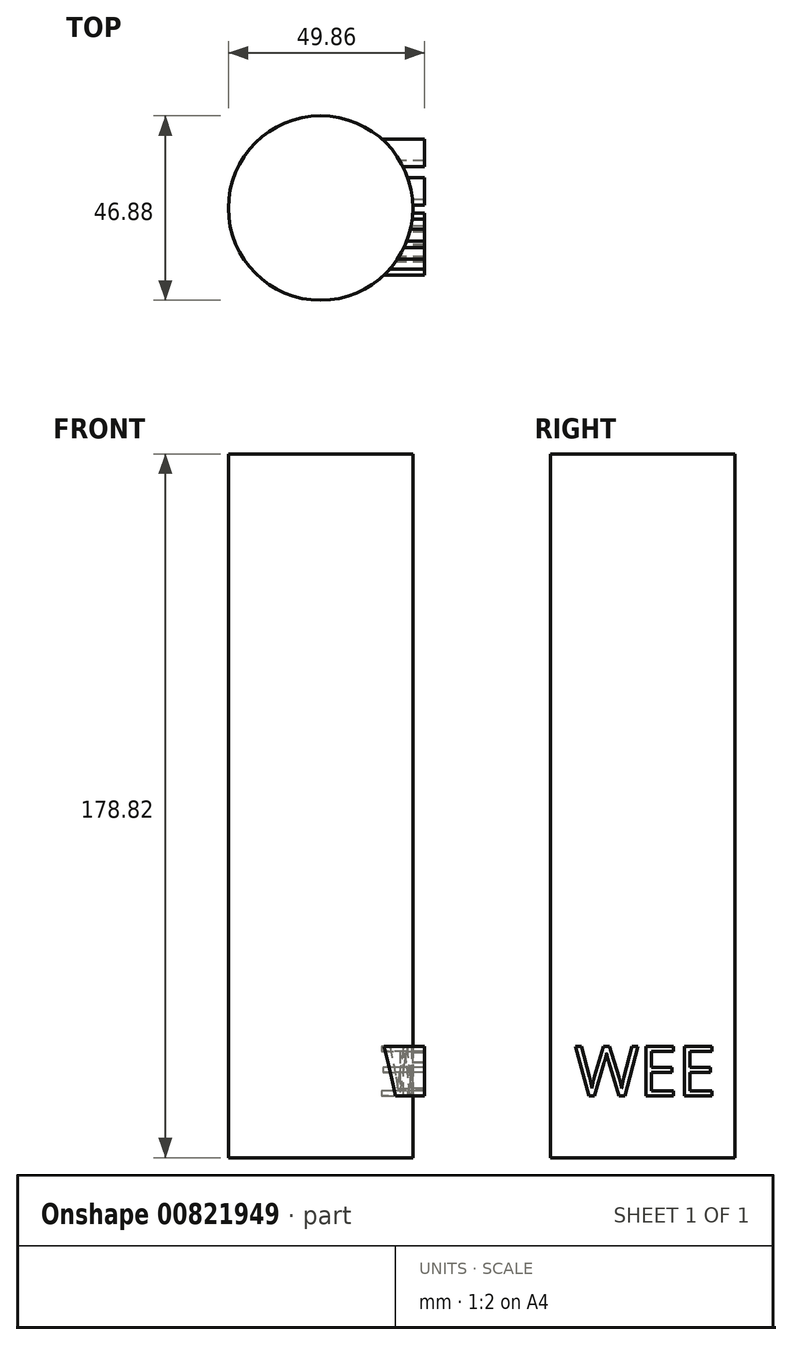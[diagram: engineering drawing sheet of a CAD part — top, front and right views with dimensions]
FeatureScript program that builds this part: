
annotation { "Feature Type Name" : "Feature", "Feature Type Description" : "" }
export const myFeature = defineFeature(function(context is Context, id is Id, definition is map)
    precondition{}
    {
        {
            var Q0;
            Q0=qCreatedBy(makeId("Top.planeOp"),FACE);
            var sketch = newSketch(context, id + "F0", { "sketchPlane" : qUnion([Q0])});
            skCircle(sketch, "E0", {"center": v(0, 0) * mm, "radius": 23.44 * mm});
            skSolve(sketch);
        }
        {
            var Q0;
            Q0 = qSketchRegion(id + "F0", true);
            extrude(context, id + "F1", {"entities" : qUnion([Q0]), "depth" : 178.82 * mm, "offsetDistance" : 25.4 * mm});
        }
        {
            var Q0;
            Q0=qCreatedBy(makeId("Right.planeOp"),FACE);
            var sketch = newSketch(context, id + "F2", { "sketchPlane" : qUnion([Q0])});
            skText(sketch, "E1", { "text": "WEE", "fontName": "OpenSans-Regular.ttf"});
            const initialGuessF2  = {"E1": [-0.01732, 0.01572, 1, 0, 0.0127]};
            skSetInitialGuess(sketch, initialGuessF2);
            skSolve(sketch);
        }
        {
            var Q0;
            Q0 = qSketchRegion(id + "F2", true);
            extrude(context, id + "F3", {"entities" : qUnion([Q0]), "operationType" : NewBodyOperationType.ADD, "depth" : 26.42 * mm, "offsetDistance" : 25.4 * mm});
        }
    });
